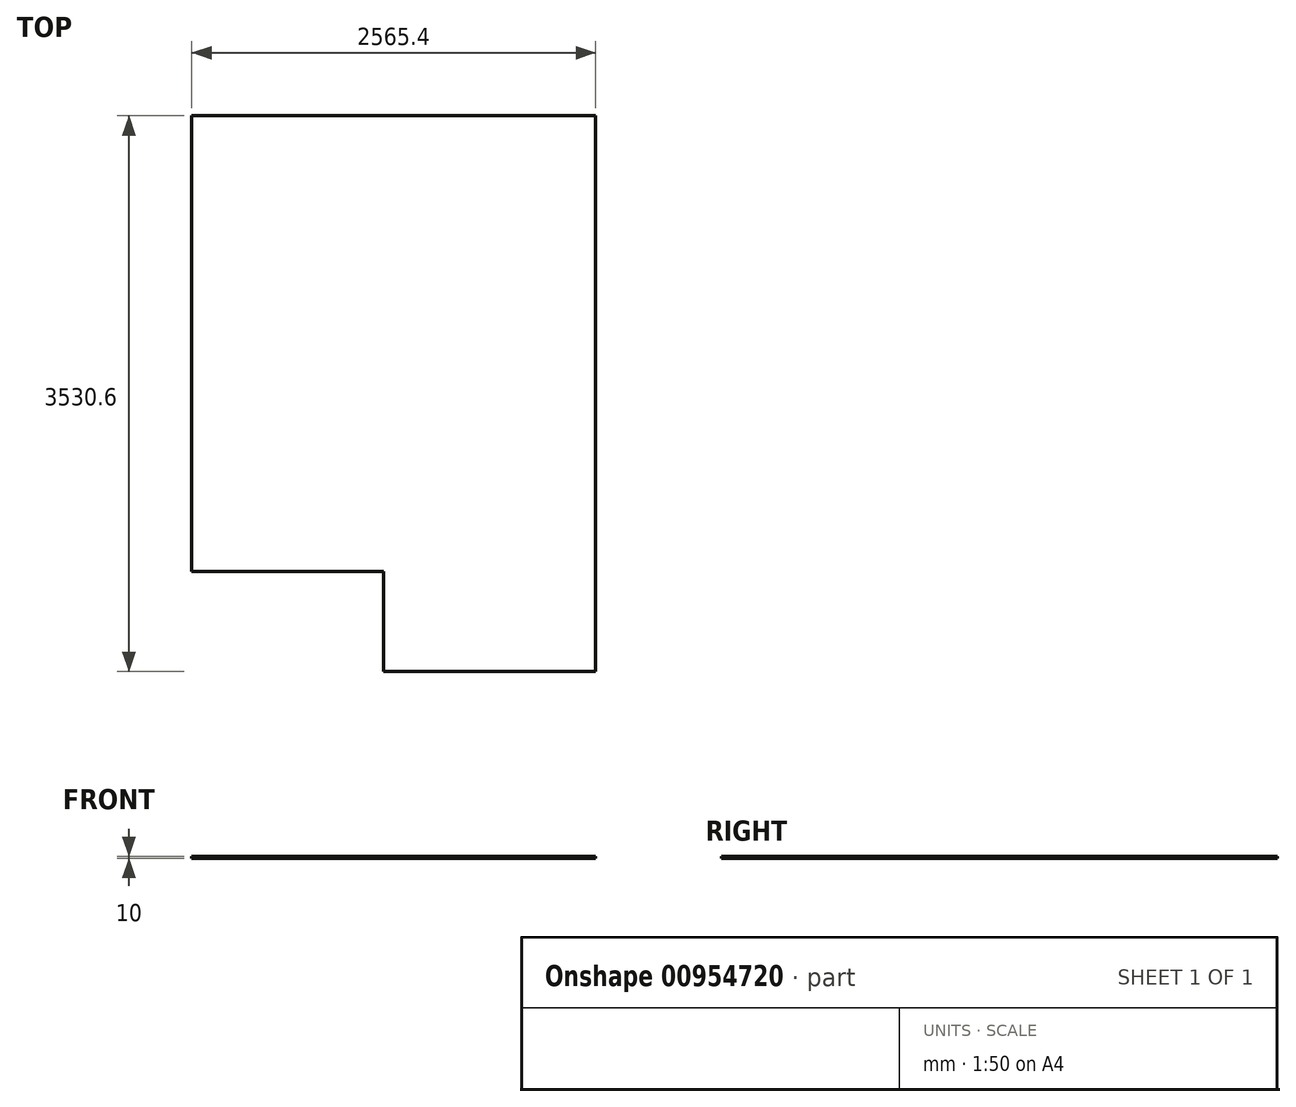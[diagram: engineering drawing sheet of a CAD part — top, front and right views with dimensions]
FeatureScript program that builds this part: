
annotation { "Feature Type Name" : "Feature", "Feature Type Description" : "" }
export const myFeature = defineFeature(function(context is Context, id is Id, definition is map)
    precondition{}
    {
        {
            var Q0;
            Q0=qCreatedBy(makeId("Top.planeOp"),FACE);
            var sketch = newSketch(context, id + "F0", { "sketchPlane" : qUnion([Q0])});
            skLineSegment(sketch, "E0", {"start": v(0, 0) * mm, "end": v(0, 3530.6) * mm});
            skLineSegment(sketch, "E1", {"start": v(0, 3530.6) * mm, "end": v(-2565.4, 3530.6) * mm});
            skLineSegment(sketch, "E2", {"start": v(-2565.4, 3530.6) * mm, "end": v(-2565.4, 635) * mm});
            skLineSegment(sketch, "E3", {"start": v(-2565.4, 635) * mm, "end": v(-1346.2, 635) * mm});
            skLineSegment(sketch, "E4", {"start": v(-1346.2, 635) * mm, "end": v(-1346.2, 0) * mm});
            skLineSegment(sketch, "E5", {"start": v(-1346.2, 0) * mm, "end": v(0, 0) * mm});
            skSolve(sketch);
        }
        {
            var Q0;
            Q0 = qSketchRegion(id + "F0", true);
            extrude(context, id + "F1", {"entities" : qUnion([Q0]), "depth" : 10 * mm, "offsetDistance" : 25.4 * mm});
        }
    });
